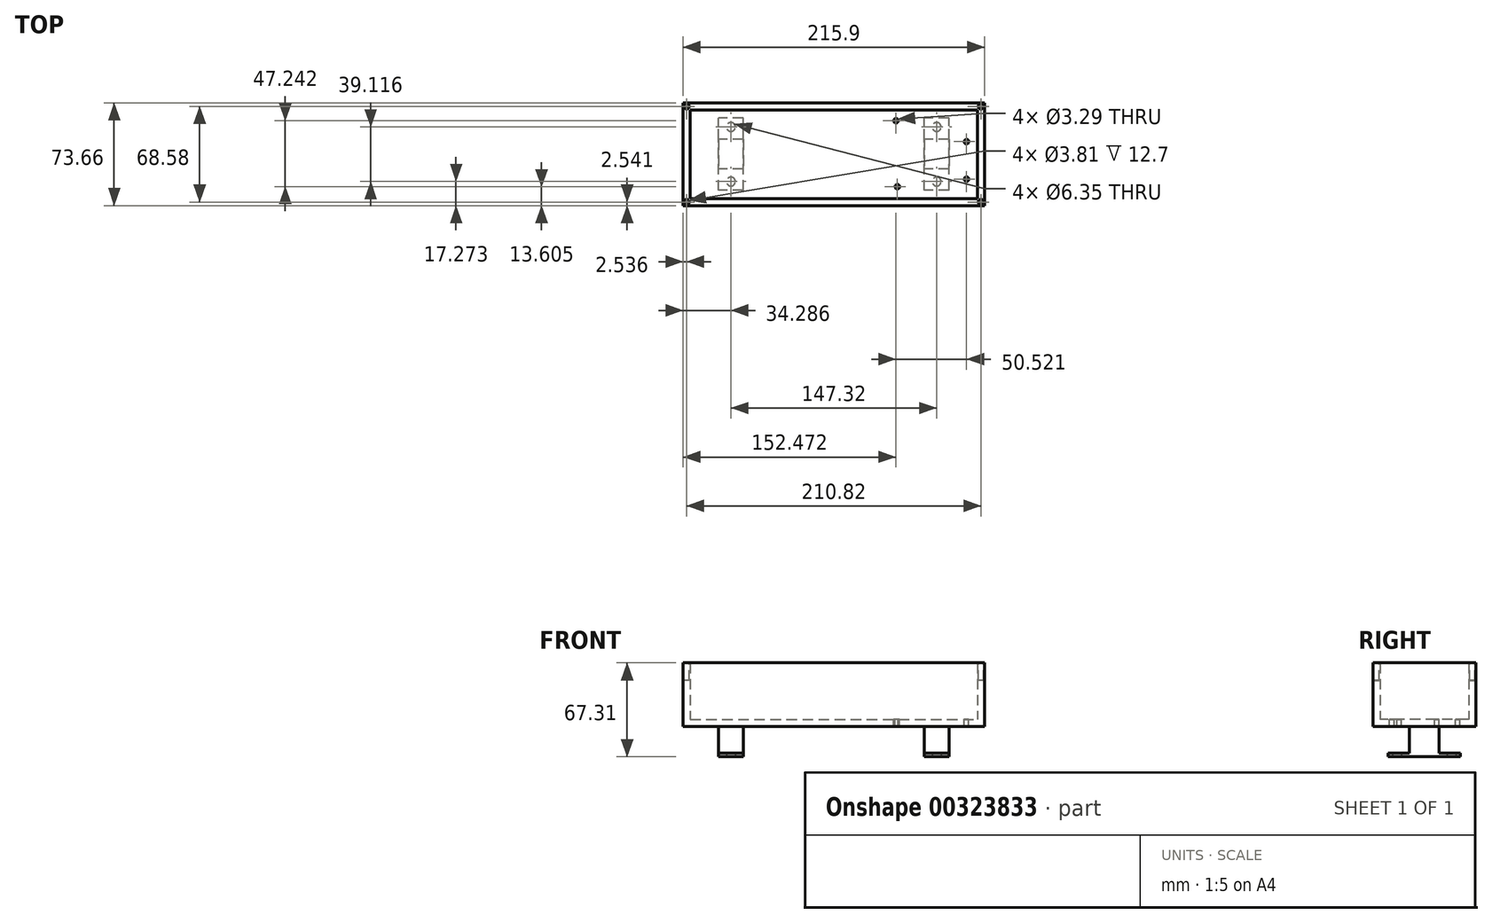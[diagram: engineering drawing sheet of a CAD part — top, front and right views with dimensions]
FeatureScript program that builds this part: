
annotation { "Feature Type Name" : "Feature", "Feature Type Description" : "" }
export const myFeature = defineFeature(function(context is Context, id is Id, definition is map)
    precondition{}
    {
        {
            var Q0;
            Q0=qCreatedBy(makeId("Top.planeOp"),FACE);
            var sketch = newSketch(context, id + "F0", { "sketchPlane" : qUnion([Q0])});
            skLineSegment(sketch, "E0.bottom", {"start": v(-52.86, 57.6) * mm, "end": v(163.04, 57.6) * mm});
            skLineSegment(sketch, "E0.top", {"start": v(-52.86, -16.07) * mm, "end": v(163.04, -16.07) * mm});
            skLineSegment(sketch, "E0.left", {"start": v(-52.86, 57.6) * mm, "end": v(-52.86, -16.07) * mm});
            skLineSegment(sketch, "E0.right", {"start": v(163.04, 57.6) * mm, "end": v(163.04, -16.07) * mm});
            skLineSegment(sketch, "E1.0", {"start": v(-47.78, 52.51) * mm, "end": v(157.96, 52.51) * mm});
            skLineSegment(sketch, "E1.1", {"start": v(-47.78, 52.51) * mm, "end": v(-47.78, -10.99) * mm});
            skLineSegment(sketch, "E1.2", {"start": v(-47.78, -10.99) * mm, "end": v(157.96, -10.99) * mm});
            skLineSegment(sketch, "E1.3", {"start": v(157.96, 52.51) * mm, "end": v(157.96, -10.99) * mm});
            skSolve(sketch);
        }
        {
            var Q0;
            Q0=makeQuery(id+"F0.imprint","IMPRINT",FACE,{"disambiguationData":[TD([[makeQuery(id+"F0.imprint","IMPRINT",EDGE,{"derivedFrom":sQuery(id+"F0.wireOp",EDGE,"E0.bottom")}),-1.0]])]});
            var Q1;
            Q1=makeQuery(id+"F0.imprint","IMPRINT",FACE,{"disambiguationData":[TD([[makeQuery(id+"F0.imprint","IMPRINT",EDGE,{"derivedFrom":sQuery(id+"F0.wireOp",EDGE,"E1.0")}),-1.0]])]});
            extrude(context, id + "F1", {"entities" : qUnion([Q0, Q1]), "oppositeDirection" : true, "depth" : 5.08 * mm});
        }
        {
            var Q0;
            Q0=makeQuery(id+"F0.imprint","IMPRINT",FACE,{"disambiguationData":[TD([[makeQuery(id+"F0.imprint","IMPRINT",EDGE,{"derivedFrom":sQuery(id+"F0.wireOp",EDGE,"E0.bottom")}),-1.0]])]});
            extrude(context, id + "F2", {"entities" : qUnion([Q0]), "operationType" : NewBodyOperationType.ADD, "depth" : 40.64 * mm});
        }
        {
            var Q0;
            Q0=makeQuery(id+"F0.imprint","IMPRINT",FACE,{"disambiguationData":[TD([[makeQuery(id+"F0.imprint","IMPRINT",EDGE,{"derivedFrom":sQuery(id+"F0.wireOp",EDGE,"E1.0")}),-1.0]])]});
            var sketch = newSketch(context, id + "F3", { "sketchPlane" : qUnion([Q0])});
            skCircle(sketch, "E2", {"center": v(150.13, 29.78) * mm, "radius": 1.64 * mm});
            skCircle(sketch, "E3", {"center": v(150.13, 2.9) * mm, "radius": 1.64 * mm});
            skCircle(sketch, "E4", {"center": v(100.6, -2.47) * mm, "radius": 1.64 * mm});
            skCircle(sketch, "E5", {"center": v(99.61, 44.78) * mm, "radius": 1.64 * mm});
            skLineSegment(sketch, "E6", {"start": v(53.24, 47.43) * mm, "end": v(152.88, 47.43) * mm, "construction": true});
            skLineSegment(sketch, "E7", {"start": v(152.88, 44.89) * mm, "end": v(152.88, 8.13) * mm, "construction": true});
            skLineSegment(sketch, "E8", {"start": v(152.88, -5) * mm, "end": v(80.42, -5) * mm, "construction": true});
            skSolve(sketch);
        }
        {
            var Q0;
            Q0=qSketchRegion(id+"F3",true);
            extrude(context, id + "F4", {"entities" : qUnion([Q0]), "operationType" : NewBodyOperationType.REMOVE, "endBound" : BoundingType.THROUGH_ALL, "oppositeDirection" : true, "depth" : 25.4 * mm});
        }
        {
            var Q0;
            Q0=makeQuery(id+"F2.opExtrude","CAP_FACE",FACE,{"disambiguationData":[OSD([sQuery(id+"F0.wireOp",EDGE,"E0.bottom"),sQuery(id+"F0.wireOp",EDGE,"E0.top"),sQuery(id+"F0.wireOp",EDGE,"E0.left"),sQuery(id+"F0.wireOp",EDGE,"E0.right"),sQuery(id+"F0.wireOp",EDGE,"E1.0"),sQuery(id+"F0.wireOp",EDGE,"E1.1"),sQuery(id+"F0.wireOp",EDGE,"E1.2"),sQuery(id+"F0.wireOp",EDGE,"E1.3")])],"isStart":false});
            var sketch = newSketch(context, id + "F5", { "sketchPlane" : qUnion([Q0])});
            skCircle(sketch, "E9", {"center": v(160.5, -13.53) * mm, "radius": 1.9 * mm});
            skCircle(sketch, "E10", {"center": v(160.5, 55.05) * mm, "radius": 1.9 * mm});
            skCircle(sketch, "E11", {"center": v(-50.32, 55.05) * mm, "radius": 1.9 * mm});
            skCircle(sketch, "E12", {"center": v(-50.32, -13.53) * mm, "radius": 1.9 * mm});
            skSolve(sketch);
        }
        {
            var Q0;
            Q0=qSketchRegion(id+"F5",true);
            extrude(context, id + "F6", {"entities" : qUnion([Q0]), "operationType" : NewBodyOperationType.REMOVE, "oppositeDirection" : true, "depth" : 12.7 * mm});
        }
        {
            var Q0;
            Q0=makeQuery(id+"F1.opExtrude","CAP_FACE",FACE,{"disambiguationData":[OSD([sQuery(id+"F0.wireOp",EDGE,"E0.bottom"),sQuery(id+"F0.wireOp",EDGE,"E0.top"),sQuery(id+"F0.wireOp",EDGE,"E0.left"),sQuery(id+"F0.wireOp",EDGE,"E0.right")])],"isStart":false});
            var sketch = newSketch(context, id + "F7", { "sketchPlane" : qUnion([Q0])});
            skLineSegment(sketch, "E13.bottom", {"start": v(137.64, -31.43) * mm, "end": v(119.86, -31.43) * mm});
            skLineSegment(sketch, "E13.top", {"start": v(137.64, -10.1) * mm, "end": v(119.86, -10.1) * mm});
            skLineSegment(sketch, "E13.left", {"start": v(137.64, -31.43) * mm, "end": v(137.64, -10.1) * mm});
            skLineSegment(sketch, "E13.right", {"start": v(119.86, -31.43) * mm, "end": v(119.86, -10.1) * mm});
            skLineSegment(sketch, "E14.bottom", {"start": v(-9.68, -31.43) * mm, "end": v(-27.46, -31.43) * mm});
            skLineSegment(sketch, "E14.top", {"start": v(-9.68, -10.1) * mm, "end": v(-27.46, -10.1) * mm});
            skLineSegment(sketch, "E14.left", {"start": v(-9.68, -31.43) * mm, "end": v(-9.68, -10.1) * mm});
            skLineSegment(sketch, "E14.right", {"start": v(-27.46, -31.43) * mm, "end": v(-27.46, -10.1) * mm});
            skLineSegment(sketch, "E15", {"start": v(137.64, -20.76) * mm, "end": v(119.86, -20.76) * mm, "construction": true});
            skLineSegment(sketch, "E16", {"start": v(-9.68, -20.76) * mm, "end": v(-27.46, -20.76) * mm, "construction": true});
            skSolve(sketch);
        }
        {
            var Q0;
            Q0=makeQuery(id+"F7.imprint","IMPRINT",FACE,{"disambiguationData":[TD([[makeQuery(id+"F7.imprint","IMPRINT",EDGE,{"derivedFrom":sQuery(id+"F7.wireOp",EDGE,"E13.bottom")}),-1.0]])]});
            var Q1;
            Q1=makeQuery(id+"F7.imprint","IMPRINT",FACE,{"disambiguationData":[TD([[makeQuery(id+"F7.imprint","IMPRINT",EDGE,{"derivedFrom":sQuery(id+"F7.wireOp",EDGE,"E14.bottom")}),-1.0]])]});
            extrude(context, id + "F8", {"entities" : qUnion([Q0, Q1]), "operationType" : NewBodyOperationType.ADD, "depth" : 19.05 * mm});
        }
        {
            var Q0;
            Q0=makeQuery(id+"F8.opExtrude","CAP_FACE",FACE,{"disambiguationData":[OSD([sQuery(id+"F7.wireOp",EDGE,"E13.bottom"),sQuery(id+"F7.wireOp",EDGE,"E13.top"),sQuery(id+"F7.wireOp",EDGE,"E13.left"),sQuery(id+"F7.wireOp",EDGE,"E13.right")])],"isStart":false});
            var sketch = newSketch(context, id + "F9", { "sketchPlane" : qUnion([Q0])});
            skLineSegment(sketch, "E17.bottom", {"start": v(137.64, 5.15) * mm, "end": v(119.86, 5.15) * mm});
            skLineSegment(sketch, "E17.top", {"start": v(137.64, -46.67) * mm, "end": v(119.86, -46.67) * mm});
            skLineSegment(sketch, "E17.left", {"start": v(137.64, 5.15) * mm, "end": v(137.64, -46.67) * mm});
            skLineSegment(sketch, "E17.right", {"start": v(119.86, 5.15) * mm, "end": v(119.86, -46.67) * mm});
            skLineSegment(sketch, "E18.bottom", {"start": v(-9.68, 5.15) * mm, "end": v(-27.46, 5.15) * mm});
            skLineSegment(sketch, "E18.top", {"start": v(-9.68, -46.67) * mm, "end": v(-27.46, -46.67) * mm});
            skLineSegment(sketch, "E18.left", {"start": v(-9.68, 5.15) * mm, "end": v(-9.68, -46.67) * mm});
            skLineSegment(sketch, "E18.right", {"start": v(-27.46, 5.15) * mm, "end": v(-27.46, -46.67) * mm});
            skLineSegment(sketch, "E19", {"start": v(137.64, -20.76) * mm, "end": v(119.86, -20.76) * mm, "construction": true});
            skLineSegment(sketch, "E20", {"start": v(-9.68, -20.76) * mm, "end": v(-27.46, -20.76) * mm, "construction": true});
            skSolve(sketch);
        }
        {
            var Q0;
            {var subQ0=sQuery(id+"F9.wireOp",EDGE,"E17.top");Q0=makeQuery(id+"F9.imprint","IMPRINT",FACE,{"disambiguationData":[TD([[makeQuery(id+"F9.imprint","IMPRINT",EDGE,{"derivedFrom":subQ0}),-1.0]])]});}
            var Q1;
            {var subQ1=makeQuery(id+"F8.opExtrude","CAP_EDGE",EDGE,{"disambiguationData":[OSD([sQuery(id+"F7.wireOp",EDGE,"E13.bottom")])],"isStart":false});Q1=makeQuery(id+"F9.imprint","IMPRINT",FACE,{"disambiguationData":[TD([[makeQuery(id+"F9.imprint","IMPRINT",EDGE,{"derivedFrom":subQ1}),-1.0]])]});}
            var Q2;
            {var subQ0=sQuery(id+"F9.wireOp",EDGE,"E17.bottom");Q2=makeQuery(id+"F9.imprint","IMPRINT",FACE,{"disambiguationData":[TD([[makeQuery(id+"F9.imprint","IMPRINT",EDGE,{"derivedFrom":subQ0}),1.0]])]});}
            var Q3;
            Q3=makeQuery(id+"F9.imprint","IMPRINT",FACE,{"disambiguationData":[TD([[makeQuery(id+"F9.imprint","IMPRINT",EDGE,{"derivedFrom":sQuery(id+"F9.wireOp",EDGE,"E18.bottom")}),1.0]])]});
            extrude(context, id + "F10", {"entities" : qUnion([Q0, Q1, Q2, Q3]), "operationType" : NewBodyOperationType.ADD, "depth" : 2.54 * mm});
        }
        {
            var Q0;
            Q0=makeQuery(id+"F10.opExtrude","CAP_FACE",FACE,{"disambiguationData":[OSD([sQuery(id+"F9.wireOp",EDGE,"E17.bottom"),sQuery(id+"F9.wireOp",EDGE,"E17.top"),sQuery(id+"F9.wireOp",EDGE,"E17.left"),sQuery(id+"F9.wireOp",EDGE,"E17.right")])],"isStart":false});
            var sketch = newSketch(context, id + "F11", { "sketchPlane" : qUnion([Q0])});
            skCircle(sketch, "E21", {"center": v(128.75, -1.2) * mm, "radius": 3.18 * mm});
            skCircle(sketch, "E22", {"center": v(128.75, -40.32) * mm, "radius": 3.18 * mm});
            skCircle(sketch, "E23", {"center": v(-18.57, -40.32) * mm, "radius": 3.18 * mm});
            skCircle(sketch, "E24", {"center": v(-18.57, -1.2) * mm, "radius": 3.18 * mm});
            skSolve(sketch);
        }
        {
            var Q0;
            Q0=makeQuery(id+"F11.imprint","IMPRINT",FACE,{"disambiguationData":[TD([[makeQuery(id+"F11.imprint","IMPRINT",EDGE,{"derivedFrom":sQuery(id+"F11.wireOp",EDGE,"E24")}),1.0]])]});
            var Q1;
            Q1=makeQuery(id+"F11.imprint","IMPRINT",FACE,{"disambiguationData":[TD([[makeQuery(id+"F11.imprint","IMPRINT",EDGE,{"derivedFrom":sQuery(id+"F11.wireOp",EDGE,"E23")}),1.0]])]});
            var Q2;
            Q2=makeQuery(id+"F11.imprint","IMPRINT",FACE,{"disambiguationData":[TD([[makeQuery(id+"F11.imprint","IMPRINT",EDGE,{"derivedFrom":sQuery(id+"F11.wireOp",EDGE,"E22")}),1.0]])]});
            var Q3;
            Q3=makeQuery(id+"F11.imprint","IMPRINT",FACE,{"disambiguationData":[TD([[makeQuery(id+"F11.imprint","IMPRINT",EDGE,{"derivedFrom":sQuery(id+"F11.wireOp",EDGE,"E21")}),1.0]])]});
            var Q4;
            {var subQ0=sQuery(id+"F9.wireOp",EDGE,"E18.bottom");var subQ1=sQuery(id+"F9.wireOp",EDGE,"E18.left");var subQ2=sQuery(id+"F9.wireOp",EDGE,"E18.right");Q4=makeQuery(id+"F10.boolean.opBoolean","SPLIT",FACE,{"disambiguationData":[TD([makeQuery(id+"F8.opExtrude","SWEPT_FACE",FACE,{"disambiguationData":[OSD([sQuery(id+"F7.wireOp",EDGE,"E14.top")])]})])],"derivedFrom":makeQuery(id+"F10.opExtrude","CAP_FACE",FACE,{"disambiguationData":[OSD([subQ0,sQuery(id+"F9.wireOp",EDGE,"E18.top"),subQ1,subQ2])],"isStart":true})});}
            extrude(context, id + "F12", {"entities" : qUnion([Q0, Q1, Q2, Q3]), "operationType" : NewBodyOperationType.REMOVE, "endBound" : BoundingType.UP_TO_SURFACE, "oppositeDirection" : true, "endBoundEntityFace" : qUnion([Q4]), "depth" : 25.4 * mm});
        }
    });
